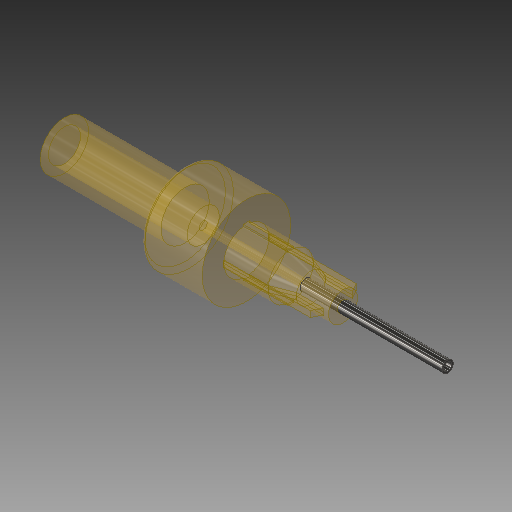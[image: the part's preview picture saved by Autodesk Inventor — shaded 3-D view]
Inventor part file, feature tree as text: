
AUTODESK INVENTOR PART (.ipt)
format: ipt  version: 2019 (Build 230136000, 136)  size: 222,208 bytes
history: native  units: mm
features: sketch x2, revolve x2, extrude x2, mirror x2, fillet x1
ambient origin geometry x8: Origin, YZ Plane, XZ Plane, XY Plane, X Axis, Y Axis, Z Axis, Center Point
bodies: Solid1 (feature_tree), Solid2 (feature_tree)
feature tree (9):
  sketch  "Sketch1"  dims[d0=11.0mm d1=7.62mm d3=25.0mm]
  revolve  "Revolution1"  [1 undecoded]
  fillet  "Fillet1"  Radius=25.0mm
  extrude  "Extrusion1"  Depth=0.75mm
  mirror  "Mirror1"
  extrude  "Extrusion2"  Depth=15.0mm
  mirror  "Mirror2"
  revolve  "Revolution2"  Angle=90.0deg
  sketch  "Sketch2"  dims[d4=6.0mm d5=4.0mm d6=15.0mm d7=90.0deg d8=1.0mm d9=0.2mm d10=0.5mm d11=5.6mm d12=5.5mm d13=3.6mm d14=4.0mm d15=12.0mm d16=0.75mm d17=0.0mm d18=0.2mm d19=0.75mm d20=0.0mm d21=90.0deg]
note: 1 required parameter value undecoded (feature->parameter linkage not recoverable at this tier; creation-order binding heuristic only, values carry confidence <= 0.55)
